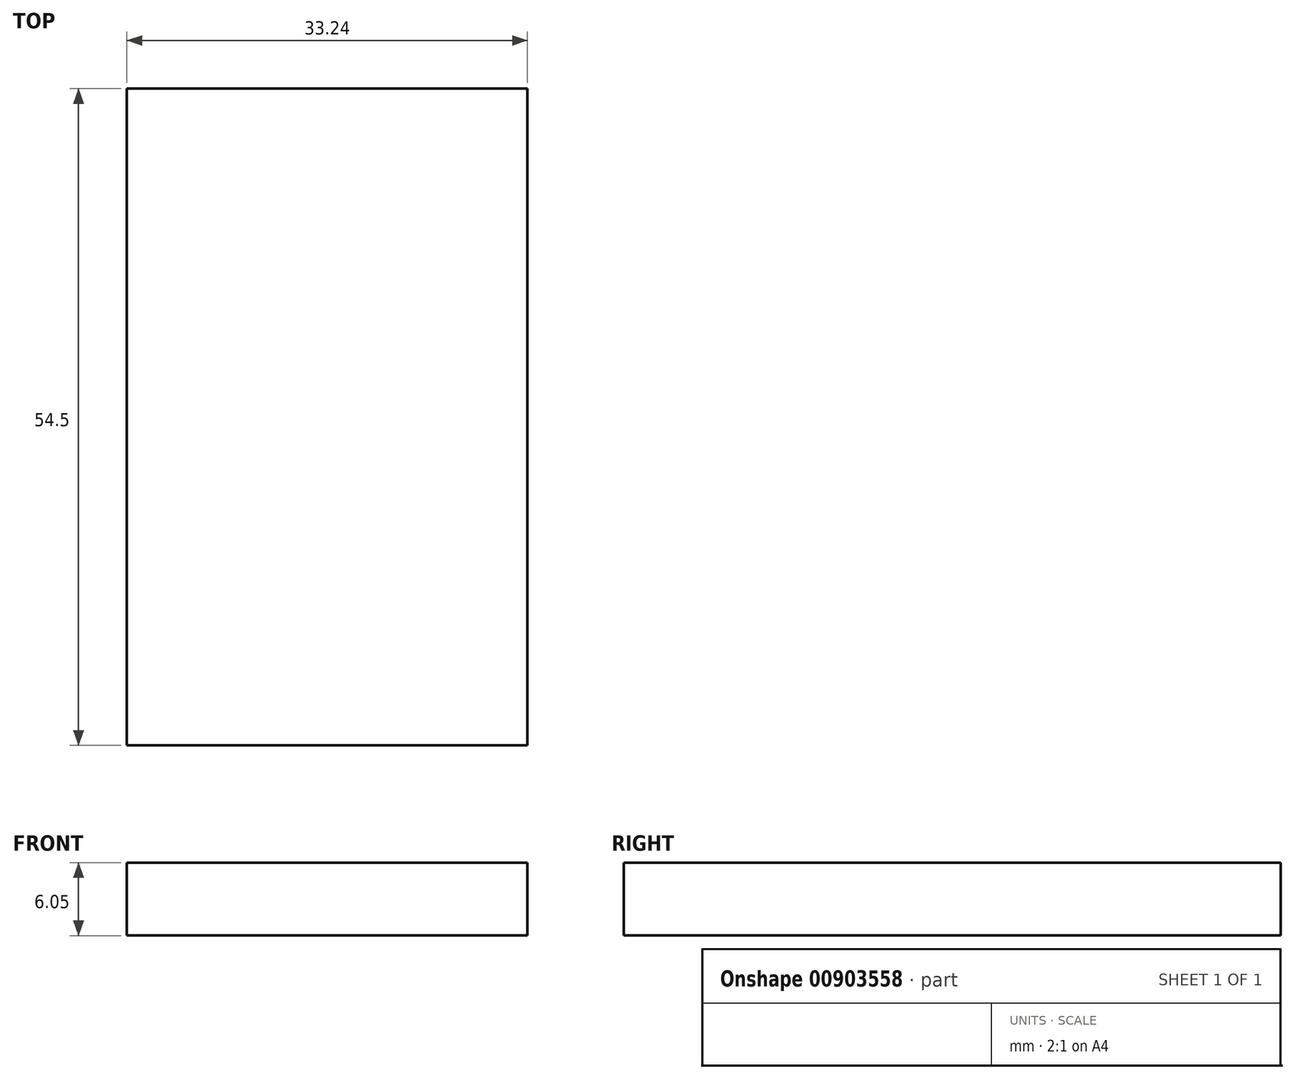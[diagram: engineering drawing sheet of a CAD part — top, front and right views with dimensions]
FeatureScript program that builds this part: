
annotation { "Feature Type Name" : "Feature", "Feature Type Description" : "" }
export const myFeature = defineFeature(function(context is Context, id is Id, definition is map)
    precondition{}
    {
        {
            var Q0;
            Q0=qCreatedBy(makeId("Top.planeOp"),FACE);
            var sketch = newSketch(context, id + "F0", { "sketchPlane" : qUnion([Q0])});
            skLineSegment(sketch, "E0.bottom", {"start": v(0, 0) * mm, "end": v(33.24, 0) * mm});
            skLineSegment(sketch, "E0.top", {"start": v(0, 54.5) * mm, "end": v(33.24, 54.5) * mm});
            skLineSegment(sketch, "E0.left", {"start": v(0, 0) * mm, "end": v(0, 54.5) * mm});
            skLineSegment(sketch, "E0.right", {"start": v(33.24, 0) * mm, "end": v(33.24, 54.5) * mm});
            skSolve(sketch);
        }
        {
            var Q0;
            Q0 = qSketchRegion(id + "F0", true);
            extrude(context, id + "F1", {"entities" : qUnion([Q0]), "oppositeDirection" : true, "depth" : 6.05 * mm, "offsetDistance" : 25.4 * mm});
        }
    });
